# Revit family: Bright 3.G
name_source: partatom
category: Lighting Fixtures
revit_build: Autodesk Revit 2017 (Build: 20170419_0315(x64)
units: mm (PartAtom-declared; Revit-internal decimal feet)

## family parameters
Cut with Voids When Loaded = Yes
Host = Face
Light Source = Yes
Part Type = Normal
Room Calculation Point = Yes
Round Connector Dimension = Use Diameter
Shared = No

## types (8) — shared parameters
Apparent Load = 0 VA
Body = L&L_Anodized aluminium
CRI = 90 (also available: CRI 80 - ref. URL Technical sheet)
Code = -
Color Filter = 16777215
Control system = -
Cutout dimensions = diam. 96 mm
Default Elevation = 1219 mm
Delivered lumen output = 508 lm (3000K, 9W, 35°, CRI 80), 410 lm (3000K, 9W, 35°, CRI 90), 282 lm (3000K, 5W, 35°, CRI 80), 228 lm (3000K, 5W, 35°, CRI 90)
Description = recessed for outdoor applications
Dimming Lamp Color Temperature Shift = <None>
Emit from Line Length = 610 mm
Energy efficiency class = A A+ A++
Geometry = Bright 3.G_mod
Height Void = 100 mm  [stored 0.328084 ft]
Height mm = 95 mm
IP = IP67
LED Colour = 3000K (also available: 2700K and 4000K - ref. URL Technical sheet)
Length mm = 112 mm  [stored 0.367454 ft]
Lens = L&L_Tempered extra-clear glass
Lumen output at source = 792 lm (3000K, 9W, CRI 80), 639 lm (3000K, 9W, CRI 90), 440 lm (3000K, 5W, CRI 80), 355 lm (3000K, 5W, CRI 90)
Manufacturer = L&L Luce&Light
Material = body in anodized aluminium, trim in AISI 316L stainless steel, screen in tempered, serigraphed-grey and transparent extra-clear glass
Model = Bright 3.G
Mounting = recessed (ceiling, wall, floor)
No. and type of led = 1 power LED High Intensity, 3-step MacAdam, 50 000h L90 B10 (Ta 25°C)
Notes = -
Power Supply = L&L_Steel inox AISI 316L
Power cables = includes 1,50 m neoprene cable, H05RN-F 2x0,75/0,75 Ø6,3 mm
Power supply = 24Vdc
Power supply unit = not included
Radius Void = 50 mm  [stored 0.164042 ft]
Tilt Angle = 90.00°
Tiltable = ±10°
Trim = L&L_Steel inox AISI 316L
URL = https://www.lucelight.it
URL Accessories and power supply units = https://www.lucelight.it
URL Catalogue = https://www.lucelight.it
URL DXF = https://www.lucelight.it
URL Description = https://www.lucelight.it
URL General code = https://www.lucelight.it
URL IES Photometric file = https://www.lucelight.it
URL Image = https://www.lucelight.it
URL Technical sheet = https://www.lucelight.it
Voltage = 24 V
Weight kg = 0.95 kg
Width mm = 112 mm  [stored 0.367454 ft]
Wiring = parallel

## per-type parameters (varying)
| type | Apparent Load Phase 1 | Optics | Photometric Web File | Power |
| Bright 3.G K 57° (3000K 5W 24Vdc) | 5 W | 57° tiltable ±10° | BRIGHT 3.G K 57° [3000K 5W 24Vdc].IES | 5W |
| Bright 3.G L 35° (3000K 5W 24Vdc) | 5 W | 35° tiltable ±10° | BRIGHT 3.G L 35° [3000K 5W 24Vdc].IES | 5W |
| Bright 3.G M 20° (3000K 5W 24Vdc) | 5 W | 20° tiltable ±10° | BRIGHT 3.G M 20° [3000K 5W 24Vdc].IES | 5W |
| Bright 3.G S 12° (3000K 5W 24Vdc) | 5 W | 12° tiltable ±10° | BRIGHT 3.G S 12° [3000K 5W 24Vdc].IES | 5W |
| Bright 3.G K 57° (3000K 9W 24Vdc) | 9 W | 57° tiltable ±10° | BRIGHT 3.G K 57° [3000K 9W 24Vdc].IES | 9W |
| Bright 3.G L 35° (3000K 9W 24Vdc) | 9 W | 35° tiltable ±10° | BRIGHT 3.G L 35° [3000K 9W 24Vdc].IES | 9W |
| Bright 3.G M 20° (3000K 9W 24Vdc) | 9 W | 20° tiltable ±10° | BRIGHT 3.G M 20° [3000K 9W 24Vdc].IES | 9W |
| Bright 3.G S 12° (3000K 9W 24Vdc) | 9 W | 12° tiltable ±10° | BRIGHT 3.G S 12° [3000K 9W 24Vdc].IES | 9W |

note: [stored X ft] marks values corroborated as IEEE doubles in the binary element streams (Revit-internal decimal feet)

## geometry (parser evidence)
native form markers: Blend x2, Sweep x7
no freeform markers — native parametric forms only
